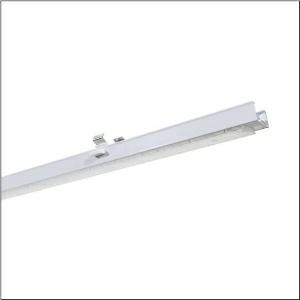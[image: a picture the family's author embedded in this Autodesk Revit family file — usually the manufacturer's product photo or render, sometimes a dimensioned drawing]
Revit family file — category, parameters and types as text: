
# Revit family: trunking_flex_31_51re11mb4cb
name_source: partatom
category: Lighting Fixtures
units: mm (PartAtom-declared; Revit-internal decimal feet)

## family parameters
Cut with Voids When Loaded = No
Host = Face
Light Source = No
Part Type = Normal
Room Calculation Point = No
Round Connector Dimension = Use Diameter
Shared = No

## types (1)
- --- (1 x LED, 11500 lm, 66 W, 4000K)
    Apparent Load = 66 VA
    CIE Flux Codes = 83 93 98 100 100
    Color Rendering = 80
    Color Temperature = 4000K
    Default Elevation = 1800 mm
    Description = Trunking Flex 31, luminaire insert, of extruded aluminium section, coated, traffic white (RAL 9016), length: 1.472mm, width: 91mm, height: 53mm, LED rated luminous flux: 11.500lm, light colour: 840, control gear: ON/OFF Multilumen, with system connector: socket, mains connection: 220..240V, AC, 50/60Hz, rated input power: 66W, luminous flux adjustable on luminaire in eight steps (3450/4380/5800/6700/8350/9200/10500/11500lm ), connected load according to luminous flux setting (19/24/32/37/47/52/60/66W), primary light control with lens, of plastic, primary optical cover: cover, of PMMA, light emission: direct distribution, protection rating (complete): IP20, insulation class (complete): insulation class I (protective earthing), certification: CE, UKCA, impact resistance: IK02, permissible ambient temperature for indoor applications: -20..+40°C, packaging unit: 1 piece
    Height = 58 mm
    Lamp = 1 x LED
    Lamp Light Flux = 11500 lm
    Lamp Power = 66 W
    Lamp count = 1
    Length = 1472 mm
    Luminous efficacy = 174 lm/W
    Manufacturer = Siteco
    ModVariant = No
    Model = 51RE11MB4CB
    Mounting Place = Ceiling
    Mounting Type = Pendant
    Number of Poles = 1
    OnlyDefault = Yes
    Power Factor = 1
    Product Name = Trunking Flex 31
    Product group = luminaire insert
    ProductGroupID = 902
    Protection Class = Protection class I
    Protection Degree = IP 20
    RLX_Detail_Level = 1
    RLX_Emergency_Light_Flux = 0 lm
    RLX_Emergency_Type = 0
    RLX_Emergency_Type_DB = No
    RlxData = <blob elided: 20953 chars, md5=f3cd6051>
    Socket = socket
    Standby Power = 0 W
    System Light Flux = 11500 lm
    System Power = 66 W
    Type Comments = factory setting: luminous flux: 100 % | (ON | ON | ON)
    Type Image = l_1266702.jpg
    URL = http://relux.com
    VarID = @adj_059258
    Voltage = 0 V
    Weight = 0.00 kg
    Width = 65 mm

## geometry (parser evidence)
native form markers: Blend x4, Sweep x13
no freeform markers — native parametric forms only
